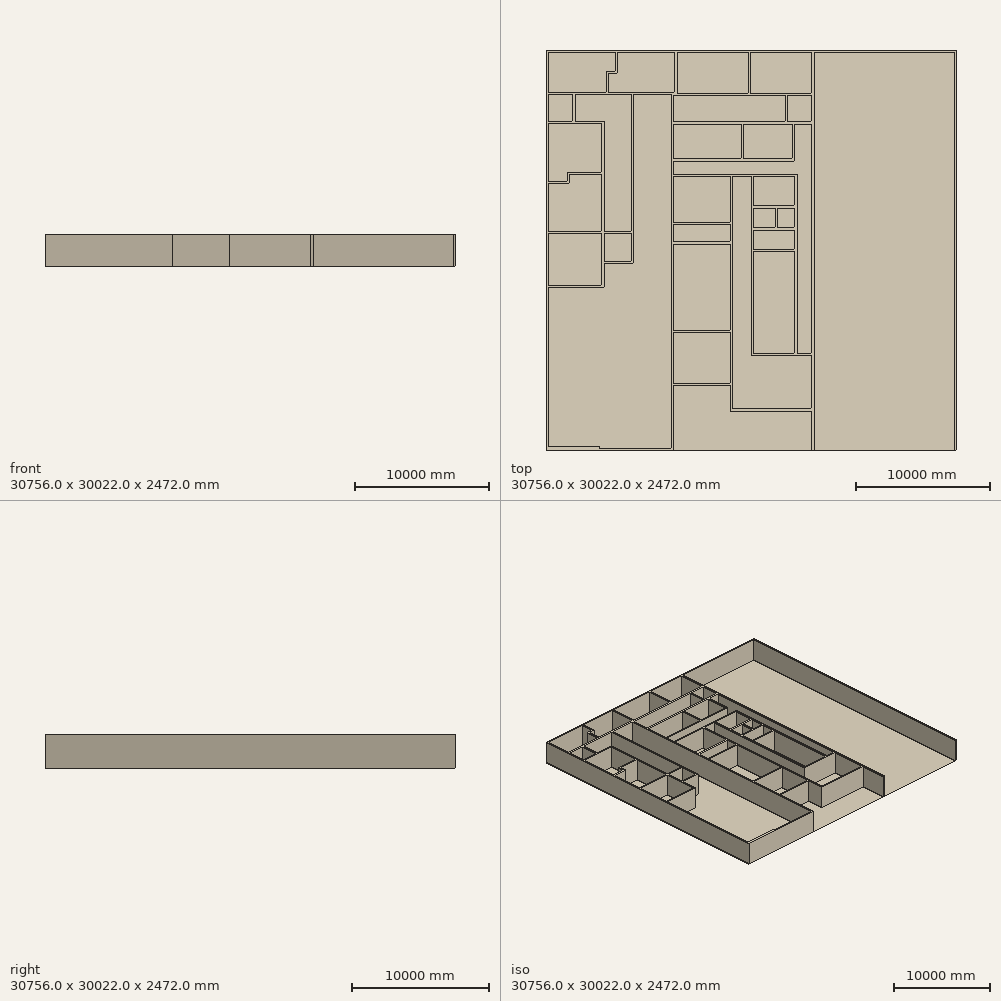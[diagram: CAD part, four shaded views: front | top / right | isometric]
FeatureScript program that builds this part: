
annotation { "Feature Type Name" : "Feature", "Feature Type Description" : "" }
export const myFeature = defineFeature(function(context is Context, id is Id, definition is map)
    precondition{}
    {
        {
            var Q0;
            Q0=qCreatedBy(makeId("Top.planeOp"),FACE);
            var sketch = newSketch(context, id + "F0", { "sketchPlane" : qUnion([Q0])});
            skLineSegment(sketch, "E0", {"start": v(4980, 2972) * mm, "end": v(683, 2972) * mm});
            skLineSegment(sketch, "E1", {"start": v(683, 2972) * mm, "end": v(683, 1419) * mm});
            skLineSegment(sketch, "E2", {"start": v(683, 1419) * mm, "end": v(0, 1419) * mm});
            skLineSegment(sketch, "E3", {"start": v(0, 1419) * mm, "end": v(0, 0) * mm});
            skLineSegment(sketch, "E4", {"start": v(0, 0) * mm, "end": v(4980, 0) * mm});
            skLineSegment(sketch, "E5", {"start": v(4980, 0) * mm, "end": v(4980, 2972) * mm});
            skLineSegment(sketch, "E6", {"start": v(515, 2972) * mm, "end": v(515, 1594) * mm});
            skLineSegment(sketch, "E7", {"start": v(515, 1594) * mm, "end": v(-168, 1594) * mm});
            skLineSegment(sketch, "E8", {"start": v(-168, 1594) * mm, "end": v(-168, 0) * mm});
            skLineSegment(sketch, "E9", {"start": v(-168, 0) * mm, "end": v(-4474, 0) * mm});
            skLineSegment(sketch, "E10", {"start": v(-4474, 0) * mm, "end": v(-4474, 2972) * mm});
            skLineSegment(sketch, "E11", {"start": v(-4474, 2972) * mm, "end": v(515, 2972) * mm});
            skLineSegment(sketch, "E12.bottom", {"start": v(-4474, -158) * mm, "end": v(-2658, -158) * mm});
            skLineSegment(sketch, "E12.top", {"start": v(-4474, -2179) * mm, "end": v(-2658, -2179) * mm});
            skLineSegment(sketch, "E12.left", {"start": v(-4474, -158) * mm, "end": v(-4474, -2179) * mm});
            skLineSegment(sketch, "E12.right", {"start": v(-2658, -158) * mm, "end": v(-2658, -2179) * mm});
            skLineSegment(sketch, "E13", {"start": v(-2451, -158) * mm, "end": v(1730, -158) * mm});
            skLineSegment(sketch, "E14", {"start": v(1730, -158) * mm, "end": v(1730, -10470) * mm});
            skLineSegment(sketch, "E15", {"start": v(1730, -10470) * mm, "end": v(-312, -10470) * mm});
            skLineSegment(sketch, "E16", {"start": v(-312, -10470) * mm, "end": v(-312, -2179) * mm});
            skLineSegment(sketch, "E17", {"start": v(-312, -2179) * mm, "end": v(-2451, -2179) * mm});
            skLineSegment(sketch, "E18", {"start": v(-2451, -2179) * mm, "end": v(-2451, -158) * mm});
            skLineSegment(sketch, "E19", {"start": v(-4474, -2347) * mm, "end": v(-487, -2347) * mm});
            skPoint(sketch, "E19.startSnap0", {"position": v(-4474, -1168.5) * mm});
            skLineSegment(sketch, "E20", {"start": v(-487, -2347) * mm, "end": v(-487, -5994) * mm});
            skLineSegment(sketch, "E21", {"start": v(-487, -5994) * mm, "end": v(-3090, -5994) * mm});
            skLineSegment(sketch, "E22", {"start": v(-3090, -5994) * mm, "end": v(-3090, -6659) * mm});
            skLineSegment(sketch, "E23", {"start": v(-3090, -6659) * mm, "end": v(-4474, -6659) * mm});
            skLineSegment(sketch, "E24", {"start": v(-4474, -6659) * mm, "end": v(-4474, -2347) * mm});
            skLineSegment(sketch, "E25", {"start": v(-4474, -6827) * mm, "end": v(-2891, -6827) * mm});
            skLineSegment(sketch, "E26", {"start": v(-2891, -6827) * mm, "end": v(-2891, -6155) * mm});
            skLineSegment(sketch, "E27", {"start": v(-2891, -6155) * mm, "end": v(-487, -6155) * mm});
            skLineSegment(sketch, "E28", {"start": v(-487, -6155) * mm, "end": v(-487, -10470) * mm});
            skLineSegment(sketch, "E29", {"start": v(-487, -10470) * mm, "end": v(-4474, -10470) * mm});
            skLineSegment(sketch, "E30", {"start": v(-4474, -10470) * mm, "end": v(-4474, -6827) * mm});
            skLineSegment(sketch, "E31", {"start": v(-4474, -6827) * mm, "end": v(-4474, -6659) * mm, "construction": true});
            skLineSegment(sketch, "E32", {"start": v(-4474, -2179) * mm, "end": v(-4474, -2347) * mm, "construction": true});
            skLineSegment(sketch, "E33", {"start": v(515, 2972) * mm, "end": v(683, 2972) * mm, "construction": true});
            skLineSegment(sketch, "E34", {"start": v(1898, -158) * mm, "end": v(4739, -158) * mm});
            skLineSegment(sketch, "E35", {"start": v(4739, -158) * mm, "end": v(4739, -26714) * mm});
            skLineSegment(sketch, "E36", {"start": v(1898, -158) * mm, "end": v(1898, -12826) * mm});
            skLineSegment(sketch, "E37", {"start": v(1898, -12826) * mm, "end": v(-311, -12826) * mm});
            skLineSegment(sketch, "E38", {"start": v(-311, -12826) * mm, "end": v(-311, -14633) * mm});
            skLineSegment(sketch, "E39", {"start": v(-311, -14633) * mm, "end": v(-4474, -14633) * mm});
            skLineSegment(sketch, "E40", {"start": v(4739, -26714) * mm, "end": v(-700, -26714) * mm});
            skLineSegment(sketch, "E41", {"start": v(-700, -26714) * mm, "end": v(-700, -26574) * mm});
            skLineSegment(sketch, "E42", {"start": v(-700, -26574) * mm, "end": v(-4474, -26574) * mm});
            skLineSegment(sketch, "E43", {"start": v(-4474, -26574) * mm, "end": v(-4474, -14633) * mm});
            skLineSegment(sketch, "E44.bottom", {"start": v(1730, -10626.5) * mm, "end": v(-312, -10626.5) * mm});
            skLineSegment(sketch, "E44.top", {"start": v(1730, -12669.5) * mm, "end": v(-312, -12669.5) * mm});
            skLineSegment(sketch, "E44.left", {"start": v(1730, -10626.5) * mm, "end": v(1730, -12669.5) * mm});
            skLineSegment(sketch, "E44.right", {"start": v(-312, -10626.5) * mm, "end": v(-312, -12669.5) * mm});
            skLineSegment(sketch, "E45.bottom", {"start": v(-4474, -10626.5) * mm, "end": v(-487, -10626.5) * mm});
            skLineSegment(sketch, "E45.top", {"start": v(-4474, -14476.5) * mm, "end": v(-487, -14476.5) * mm});
            skLineSegment(sketch, "E45.left", {"start": v(-4474, -10626.5) * mm, "end": v(-4474, -14476.5) * mm});
            skLineSegment(sketch, "E45.right", {"start": v(-487, -10626.5) * mm, "end": v(-487, -14476.5) * mm});
            skLineSegment(sketch, "E46", {"start": v(-4474, -10470) * mm, "end": v(-4474, -10626.5) * mm, "construction": true});
            skLineSegment(sketch, "E47", {"start": v(-4474, -14633) * mm, "end": v(-4474, -14476.5) * mm, "construction": true});
            skLineSegment(sketch, "E48", {"start": v(-312, -12669.5) * mm, "end": v(-311, -12826) * mm, "construction": true});
            skLineSegment(sketch, "E49", {"start": v(-312, -10470) * mm, "end": v(-312, -10626.5) * mm, "construction": true});
            skLineSegment(sketch, "E50.bottom", {"start": v(4907, -239) * mm, "end": v(13273, -239) * mm});
            skLineSegment(sketch, "E50.top", {"start": v(4907, -2227) * mm, "end": v(13273, -2227) * mm});
            skLineSegment(sketch, "E50.left", {"start": v(4907, -239) * mm, "end": v(4907, -2227) * mm});
            skLineSegment(sketch, "E50.right", {"start": v(13273, -239) * mm, "end": v(13273, -2227) * mm});
            skLineSegment(sketch, "E51.bottom", {"start": v(5148, 2972) * mm, "end": v(10481.27, 2972) * mm});
            skLineSegment(sketch, "E51.top", {"start": v(5148, -71) * mm, "end": v(10481.27, -71) * mm});
            skLineSegment(sketch, "E51.left", {"start": v(5148, 2972) * mm, "end": v(5148, -71) * mm});
            skLineSegment(sketch, "E51.right", {"start": v(10481.27, 2972) * mm, "end": v(10481.27, -71) * mm});
            skLineSegment(sketch, "E52.bottom", {"start": v(10649.27, 2972) * mm, "end": v(15261, 2972) * mm});
            skLineSegment(sketch, "E52.top", {"start": v(10649.27, -71) * mm, "end": v(15261, -71) * mm});
            skLineSegment(sketch, "E52.left", {"start": v(10649.27, 2972) * mm, "end": v(10649.27, -71) * mm});
            skLineSegment(sketch, "E52.right", {"start": v(15261, 2972) * mm, "end": v(15261, -71) * mm});
            skLineSegment(sketch, "E53.bottom", {"start": v(15261, -239) * mm, "end": v(13441, -239) * mm});
            skLineSegment(sketch, "E53.top", {"start": v(15261, -2227) * mm, "end": v(13441, -2227) * mm});
            skLineSegment(sketch, "E53.left", {"start": v(15261, -239) * mm, "end": v(15261, -2227) * mm});
            skLineSegment(sketch, "E53.right", {"start": v(13441, -239) * mm, "end": v(13441, -2227) * mm});
            skLineSegment(sketch, "E54.bottom", {"start": v(4907, -2395) * mm, "end": v(10000.74, -2395) * mm});
            skLineSegment(sketch, "E54.top", {"start": v(4907, -4993) * mm, "end": v(10000.74, -4993) * mm});
            skLineSegment(sketch, "E54.left", {"start": v(4907, -2395) * mm, "end": v(4907, -4993) * mm});
            skLineSegment(sketch, "E54.right", {"start": v(10000.74, -2395) * mm, "end": v(10000.74, -4993) * mm});
            skLineSegment(sketch, "E55.bottom", {"start": v(10168.74, -2395) * mm, "end": v(13778, -2395) * mm});
            skLineSegment(sketch, "E55.top", {"start": v(10168.74, -4993) * mm, "end": v(13778, -4993) * mm});
            skLineSegment(sketch, "E55.left", {"start": v(10168.74, -2395) * mm, "end": v(10168.74, -4993) * mm});
            skLineSegment(sketch, "E55.right", {"start": v(13778, -2395) * mm, "end": v(13778, -4993) * mm});
            skLineSegment(sketch, "E56", {"start": v(15261, -2395) * mm, "end": v(15261, -19605) * mm});
            skPoint(sketch, "E56.startSnap0", {"position": v(15261, -1233) * mm});
            skLineSegment(sketch, "E57", {"start": v(4980, 2972) * mm, "end": v(5148, 2972) * mm, "construction": true});
            skLineSegment(sketch, "E58", {"start": v(10481.27, 2972) * mm, "end": v(10649.27, 2972) * mm, "construction": true});
            skLineSegment(sketch, "E59", {"start": v(10481.27, -71) * mm, "end": v(10481.27, -239) * mm, "construction": true});
            skLineSegment(sketch, "E60", {"start": v(4907, -2227) * mm, "end": v(4907, -2395) * mm, "construction": true});
            skLineSegment(sketch, "E61", {"start": v(10000.74, -2395) * mm, "end": v(10168.74, -2395) * mm, "construction": true});
            skLineSegment(sketch, "E62", {"start": v(13273, -239) * mm, "end": v(13441, -239) * mm, "construction": true});
            skLineSegment(sketch, "E63", {"start": v(4907, -4993) * mm, "end": v(4739, -4993) * mm, "construction": true});
            skLineSegment(sketch, "E64", {"start": v(15261, -2395) * mm, "end": v(13946, -2395) * mm});
            skLineSegment(sketch, "E65", {"start": v(13946, -2395) * mm, "end": v(13946, -5161) * mm});
            skLineSegment(sketch, "E66", {"start": v(13946, -5161) * mm, "end": v(4907, -5161) * mm});
            skLineSegment(sketch, "E67", {"start": v(4907, -5161) * mm, "end": v(4907, -6175) * mm});
            skLineSegment(sketch, "E68", {"start": v(14166, -19605) * mm, "end": v(15261, -19605) * mm});
            skLineSegment(sketch, "E69", {"start": v(4907, -4993) * mm, "end": v(4907, -5161) * mm, "construction": true});
            skLineSegment(sketch, "E70", {"start": v(13778, -2395) * mm, "end": v(13946, -2395) * mm, "construction": true});
            skLineSegment(sketch, "E71", {"start": v(4907, -6175) * mm, "end": v(14166, -6175) * mm});
            skLineSegment(sketch, "E72", {"start": v(14166, -6175) * mm, "end": v(14166, -19605) * mm});
            skLineSegment(sketch, "E73.bottom", {"start": v(4907, -6343) * mm, "end": v(9130, -6343) * mm});
            skLineSegment(sketch, "E73.top", {"start": v(4907, -9788.73) * mm, "end": v(9130, -9788.73) * mm});
            skLineSegment(sketch, "E73.left", {"start": v(4907, -6343) * mm, "end": v(4907, -9788.73) * mm});
            skLineSegment(sketch, "E73.right", {"start": v(9130, -6343) * mm, "end": v(9130, -9788.73) * mm});
            skLineSegment(sketch, "E74.bottom", {"start": v(9130, -9956.73) * mm, "end": v(4907, -9956.73) * mm});
            skLineSegment(sketch, "E74.top", {"start": v(9130, -11220.78) * mm, "end": v(4907, -11220.78) * mm});
            skLineSegment(sketch, "E74.left", {"start": v(9130, -9956.73) * mm, "end": v(9130, -11220.78) * mm});
            skLineSegment(sketch, "E74.right", {"start": v(4907, -9956.73) * mm, "end": v(4907, -11220.78) * mm});
            skLineSegment(sketch, "E75.bottom", {"start": v(4907, -11388.78) * mm, "end": v(9130, -11388.78) * mm});
            skLineSegment(sketch, "E75.top", {"start": v(4907, -17885) * mm, "end": v(9130, -17885) * mm});
            skLineSegment(sketch, "E75.left", {"start": v(4907, -11388.78) * mm, "end": v(4907, -17885) * mm});
            skLineSegment(sketch, "E75.right", {"start": v(9130, -11388.78) * mm, "end": v(9130, -17885) * mm});
            skLineSegment(sketch, "E76.bottom", {"start": v(4907, -18053) * mm, "end": v(9130, -18053) * mm});
            skLineSegment(sketch, "E76.top", {"start": v(4907, -21828) * mm, "end": v(9130, -21828) * mm});
            skLineSegment(sketch, "E76.left", {"start": v(4907, -18053) * mm, "end": v(4907, -21828) * mm});
            skLineSegment(sketch, "E76.right", {"start": v(9130, -18053) * mm, "end": v(9130, -21828) * mm});
            skLineSegment(sketch, "E77", {"start": v(9298, -6343) * mm, "end": v(9298, -23758) * mm});
            skLineSegment(sketch, "E78", {"start": v(9298, -23758) * mm, "end": v(15261, -23758) * mm});
            skLineSegment(sketch, "E79", {"start": v(15261, -23758) * mm, "end": v(15261, -19773) * mm});
            skLineSegment(sketch, "E80", {"start": v(15261, -19773) * mm, "end": v(10725, -19773) * mm});
            skLineSegment(sketch, "E81", {"start": v(10725, -19773) * mm, "end": v(10725, -6343) * mm});
            skLineSegment(sketch, "E82", {"start": v(10725, -6343) * mm, "end": v(9298, -6343) * mm});
            skLineSegment(sketch, "E83.bottom", {"start": v(10893, -6343) * mm, "end": v(13998, -6343) * mm});
            skLineSegment(sketch, "E83.top", {"start": v(10893, -8516.18) * mm, "end": v(13998, -8516.18) * mm});
            skLineSegment(sketch, "E83.left", {"start": v(10893, -6343) * mm, "end": v(10893, -8516.18) * mm});
            skLineSegment(sketch, "E83.right", {"start": v(13998, -6343) * mm, "end": v(13998, -8516.18) * mm});
            skLineSegment(sketch, "E84.bottom", {"start": v(10893, -8684.18) * mm, "end": v(12517.52, -8684.18) * mm});
            skLineSegment(sketch, "E84.top", {"start": v(10893, -10178.31) * mm, "end": v(12517.52, -10178.31) * mm});
            skLineSegment(sketch, "E84.left", {"start": v(10893, -8684.18) * mm, "end": v(10893, -10178.31) * mm});
            skLineSegment(sketch, "E84.right", {"start": v(12517.52, -8684.18) * mm, "end": v(12517.52, -10178.31) * mm});
            skLineSegment(sketch, "E85.bottom", {"start": v(13998, -8684.18) * mm, "end": v(12685.52, -8684.18) * mm});
            skLineSegment(sketch, "E85.top", {"start": v(13998, -10178.31) * mm, "end": v(12685.52, -10178.31) * mm});
            skLineSegment(sketch, "E85.left", {"start": v(13998, -8684.18) * mm, "end": v(13998, -10178.31) * mm});
            skLineSegment(sketch, "E85.right", {"start": v(12685.52, -8684.18) * mm, "end": v(12685.52, -10178.31) * mm});
            skLineSegment(sketch, "E86.bottom", {"start": v(10893, -10346.31) * mm, "end": v(13998, -10346.31) * mm});
            skLineSegment(sketch, "E86.top", {"start": v(10893, -11802.09) * mm, "end": v(13998, -11802.09) * mm});
            skLineSegment(sketch, "E86.left", {"start": v(10893, -10346.31) * mm, "end": v(10893, -11802.09) * mm});
            skLineSegment(sketch, "E86.right", {"start": v(13998, -10346.31) * mm, "end": v(13998, -11802.09) * mm});
            skLineSegment(sketch, "E87.bottom", {"start": v(10893, -11970.09) * mm, "end": v(13998, -11970.09) * mm});
            skLineSegment(sketch, "E87.top", {"start": v(10893, -19605) * mm, "end": v(13998, -19605) * mm});
            skLineSegment(sketch, "E87.left", {"start": v(10893, -11970.09) * mm, "end": v(10893, -19605) * mm});
            skLineSegment(sketch, "E87.right", {"start": v(13998, -11970.09) * mm, "end": v(13998, -19605) * mm});
            skLineSegment(sketch, "E88", {"start": v(4907, -9788.73) * mm, "end": v(4907, -9956.73) * mm, "construction": true});
            skLineSegment(sketch, "E89", {"start": v(4907, -11220.78) * mm, "end": v(4907, -11388.78) * mm, "construction": true});
            skLineSegment(sketch, "E90", {"start": v(4907, -17885) * mm, "end": v(4907, -18053) * mm, "construction": true});
            skLineSegment(sketch, "E91", {"start": v(9130, -6343) * mm, "end": v(9298, -6343) * mm, "construction": true});
            skLineSegment(sketch, "E92", {"start": v(10725, -6343) * mm, "end": v(10893, -6343) * mm, "construction": true});
            skLineSegment(sketch, "E93", {"start": v(13998, -6343) * mm, "end": v(14166, -6343) * mm, "construction": true});
            skLineSegment(sketch, "E94", {"start": v(10893, -8516.18) * mm, "end": v(10893, -8684.18) * mm, "construction": true});
            skLineSegment(sketch, "E95", {"start": v(10893, -10178.31) * mm, "end": v(10893, -10346.31) * mm, "construction": true});
            skLineSegment(sketch, "E96", {"start": v(10893, -11802.09) * mm, "end": v(10893, -11970.09) * mm, "construction": true});
            skLineSegment(sketch, "E97", {"start": v(12685.52, -10178.31) * mm, "end": v(12517.52, -10178.31) * mm, "construction": true});
            skLineSegment(sketch, "E98", {"start": v(15261, -19605) * mm, "end": v(15261, -19773) * mm, "construction": true});
            skLineSegment(sketch, "E99", {"start": v(10893, -19605) * mm, "end": v(10893, -19773) * mm, "construction": true});
            skLineSegment(sketch, "E100", {"start": v(4907, -6175) * mm, "end": v(4907, -6343) * mm, "construction": true});
            skLineSegment(sketch, "E101", {"start": v(-4642, 3140) * mm, "end": v(26114, 3140) * mm});
            skLineSegment(sketch, "E102", {"start": v(26114, 3140) * mm, "end": v(26114, -26882) * mm});
            skLineSegment(sketch, "E103", {"start": v(26114, -26882) * mm, "end": v(25946, -26882) * mm});
            skLineSegment(sketch, "E104", {"start": v(25946, -26882) * mm, "end": v(25946, 2972) * mm});
            skLineSegment(sketch, "E105", {"start": v(25946, 2972) * mm, "end": v(15429, 2972) * mm});
            skLineSegment(sketch, "E106", {"start": v(15429, 2972) * mm, "end": v(15429, -26882) * mm});
            skLineSegment(sketch, "E107", {"start": v(15429, -26882) * mm, "end": v(15261, -26882) * mm});
            skLineSegment(sketch, "E108", {"start": v(15261, -26882) * mm, "end": v(15261, -23926) * mm});
            skLineSegment(sketch, "E109", {"start": v(15261, -23926) * mm, "end": v(9130, -23926) * mm});
            skLineSegment(sketch, "E110", {"start": v(9130, -23926) * mm, "end": v(9130, -21996) * mm});
            skLineSegment(sketch, "E111", {"start": v(9130, -21996) * mm, "end": v(4907, -21996) * mm});
            skLineSegment(sketch, "E112", {"start": v(4907, -21996) * mm, "end": v(4907, -26882) * mm});
            skLineSegment(sketch, "E113", {"start": v(4907, -26882) * mm, "end": v(-4642, -26882) * mm});
            skLineSegment(sketch, "E114", {"start": v(-4642, -26882) * mm, "end": v(-4642, 3140) * mm});
            skLineSegment(sketch, "E115", {"start": v(-4474, 2972) * mm, "end": v(-4642, 2972) * mm, "construction": true});
            skLineSegment(sketch, "E116", {"start": v(4739, -26714) * mm, "end": v(4739, -26882) * mm, "construction": true});
            skLineSegment(sketch, "E117", {"start": v(4907, -21996) * mm, "end": v(4907, -21828) * mm, "construction": true});
            skLineSegment(sketch, "E118", {"start": v(15261, -23758) * mm, "end": v(15261, -23926) * mm, "construction": true});
            skLineSegment(sketch, "E119", {"start": v(9298, -23758) * mm, "end": v(9130, -23758) * mm, "construction": true});
            skLineSegment(sketch, "E120", {"start": v(25946, 2972) * mm, "end": v(25946, 3140) * mm, "construction": true});
            skSolve(sketch);
        }
        {
            var Q0;
            Q0=makeQuery(id+"F0.imprint","IMPRINT",FACE,{"disambiguationData":[TD([[makeQuery(id+"F0.imprint","IMPRINT",EDGE,{"derivedFrom":sQuery(id+"F0.wireOp",EDGE,"E0")}),-1.0]])]});
            extrude(context, id + "F1", {"entities" : qUnion([Q0]), "depth" : 2447 * mm});
        }
        {
            var Q0;
            Q0=makeQuery(id+"F0.imprint","IMPRINT",FACE,{"disambiguationData":[TD([[makeQuery(id+"F0.imprint","IMPRINT",EDGE,{"derivedFrom":sQuery(id+"F0.wireOp",EDGE,"E0")}),-1.0]])]});
            var sketch = newSketch(context, id + "F2", { "sketchPlane" : qUnion([Q0])});
            skPoint(sketch, "E121.0", {"position": v(26114, 3140) * mm});
            skPoint(sketch, "E121.1", {"position": v(-4642, -26882) * mm});
            skLineSegment(sketch, "E122.bottom", {"start": v(-4642, -26882) * mm, "end": v(26114, -26882) * mm});
            skLineSegment(sketch, "E122.top", {"start": v(-4642, 3140) * mm, "end": v(26114, 3140) * mm});
            skLineSegment(sketch, "E122.left", {"start": v(-4642, -26882) * mm, "end": v(-4642, 3140) * mm});
            skLineSegment(sketch, "E122.right", {"start": v(26114, -26882) * mm, "end": v(26114, 3140) * mm});
            skSolve(sketch);
        }
        {
            var Q0;
            Q0 = qSketchRegion(id + "F2", true);
            extrude(context, id + "F3", {"entities" : qUnion([Q0]), "oppositeDirection" : true, "depth" : 25 * mm});
        }
    });
